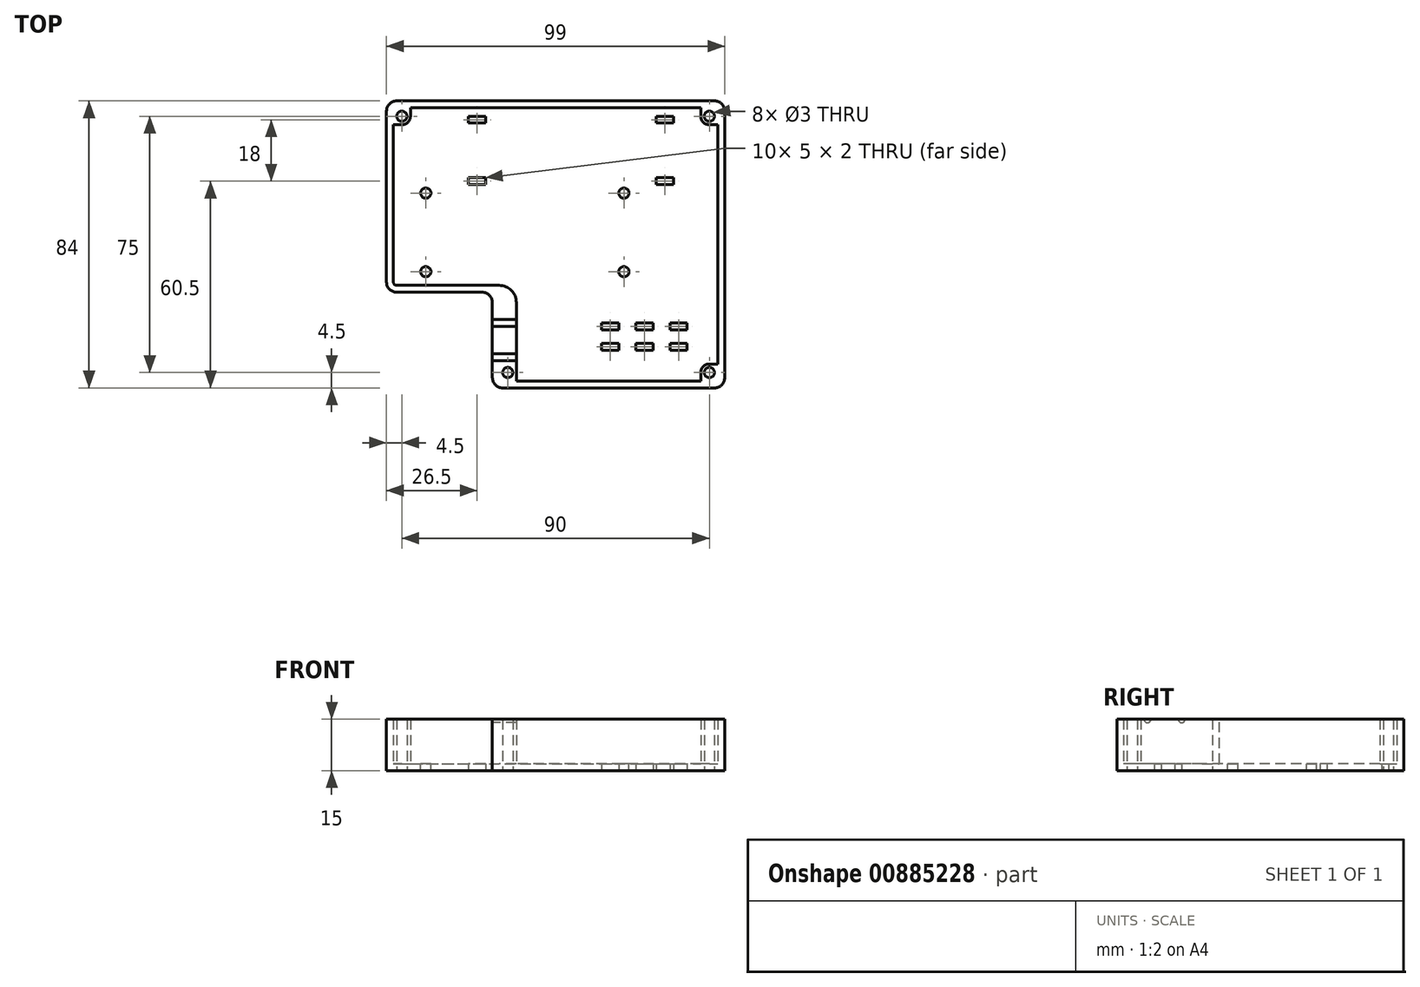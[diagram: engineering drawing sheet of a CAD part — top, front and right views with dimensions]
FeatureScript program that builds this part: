
annotation { "Feature Type Name" : "Feature", "Feature Type Description" : "" }
export const myFeature = defineFeature(function(context is Context, id is Id, definition is map)
    precondition{}
    {
        {
            var Q0;
            Q0=qCreatedBy(makeId("Top.planeOp"),FACE);
            var sketch = newSketch(context, id + "F0", { "sketchPlane" : qUnion([Q0])});
            skLineSegment(sketch, "E0.bottom", {"start": v(37.5, 17.5) * mm, "end": v(-37.5, 17.5) * mm});
            skLineSegment(sketch, "E0.left", {"start": v(40.5, 14.5) * mm, "end": v(40.5, -14.5) * mm});
            skLineSegment(sketch, "E0.right", {"start": v(-40.5, 14.5) * mm, "end": v(-40.5, -14.5) * mm});
            skPoint(sketch, "E0.middle", {"position": v(0, 0) * mm});
            skPoint(sketch, "E1.visualSharp", {"position": v(40.5, -17.5) * mm});
            skArc(sketch, "E1.filletArc", {"start": v(37.5, -17.5) * mm, "mid": v(39.62, -16.62) * mm, "end": v(40.5, -14.5) * mm});
            skPoint(sketch, "E2.visualSharp", {"position": v(40.5, 17.5) * mm});
            skArc(sketch, "E2.filletArc", {"start": v(40.5, 14.5) * mm, "mid": v(39.62, 16.62) * mm, "end": v(37.5, 17.5) * mm});
            skPoint(sketch, "E3.visualSharp", {"position": v(-40.5, -17.5) * mm});
            skArc(sketch, "E3.filletArc", {"start": v(-40.5, -14.5) * mm, "mid": v(-39.62, -16.62) * mm, "end": v(-37.5, -17.5) * mm});
            skPoint(sketch, "E4.visualSharp", {"position": v(-40.5, 17.5) * mm});
            skArc(sketch, "E4.filletArc", {"start": v(-37.5, 17.5) * mm, "mid": v(-39.62, 16.62) * mm, "end": v(-40.5, 14.5) * mm});
            skLineSegment(sketch, "E5", {"start": v(58.5, 35.5) * mm, "end": v(58.5, -42.5) * mm});
            skLineSegment(sketch, "E6", {"start": v(-37.5, 38.5) * mm, "end": v(55.5, 38.5) * mm});
            skLineSegment(sketch, "E7", {"start": v(55.5, -45.5) * mm, "end": v(-6.5, -45.5) * mm});
            skLineSegment(sketch, "E8", {"start": v(-9.5, -20.5) * mm, "end": v(-9.5, -42.5) * mm});
            skLineSegment(sketch, "E9", {"start": v(-40.5, 35.5) * mm, "end": v(-40.5, 14.5) * mm});
            skPoint(sketch, "E10.visualSharp", {"position": v(-40.5, 38.5) * mm});
            skArc(sketch, "E10.filletArc", {"start": v(-37.5, 38.5) * mm, "mid": v(-39.62, 37.62) * mm, "end": v(-40.5, 35.5) * mm});
            skPoint(sketch, "E11.visualSharp", {"position": v(58.5, 38.5) * mm});
            skArc(sketch, "E11.filletArc", {"start": v(58.5, 35.5) * mm, "mid": v(57.62, 37.62) * mm, "end": v(55.5, 38.5) * mm});
            skPoint(sketch, "E12.visualSharp", {"position": v(58.5, -45.5) * mm});
            skArc(sketch, "E12.filletArc", {"start": v(55.5, -45.5) * mm, "mid": v(57.62, -44.62) * mm, "end": v(58.5, -42.5) * mm});
            skPoint(sketch, "E13.visualSharp", {"position": v(-9.5, -45.5) * mm});
            skArc(sketch, "E13.filletArc", {"start": v(-9.5, -42.5) * mm, "mid": v(-8.62, -44.62) * mm, "end": v(-6.5, -45.5) * mm});
            skLineSegment(sketch, "E14", {"start": v(-9.5, -17.5) * mm, "end": v(37.5, -17.5) * mm, "construction": true});
            skLineSegment(sketch, "E15", {"start": v(-37.5, -17.5) * mm, "end": v(-12.5, -17.5) * mm});
            skPoint(sketch, "E16.visualSharp", {"position": v(-9.5, -17.5) * mm});
            skArc(sketch, "E16.filletArc", {"start": v(-9.5, -20.5) * mm, "mid": v(-10.38, -18.38) * mm, "end": v(-12.5, -17.5) * mm});
            skSolve(sketch);
        }
        {
            var Q0;
            Q0 = qSketchRegion(id + "F0", true);
            extrude(context, id + "F1", {"entities" : qUnion([Q0]), "depth" : 15 * mm, "offsetDistance" : 25 * mm});
        }
        {
            var Q0;
            Q0=makeQuery(id+"F1.opExtrude","CAP_FACE",FACE,{"disambiguationData":[OSD([sQuery(id+"F0.wireOp",EDGE,"E0.bottom"),sQuery(id+"F0.wireOp",EDGE,"E0.top"),sQuery(id+"F0.wireOp",EDGE,"E0.left"),sQuery(id+"F0.wireOp",EDGE,"E0.right")])],"isStart":false});
            shell(context, id + "F2", {"entities" : qUnion([Q0]), "thickness" : 2 * mm});
        }
        {
            var Q0;
            Q0=makeQuery(id+"F2.opShell","OFFSET_FACE",FACE,{"disambiguationData":[OSD([sQuery(id+"F0.wireOp",EDGE,"E0.top"),sQuery(id+"F0.wireOp",EDGE,"E0.right"),sQuery(id+"F0.wireOp",EDGE,"E3.filletArc"),sQuery(id+"F0.wireOp",EDGE,"E5"),sQuery(id+"F0.wireOp",EDGE,"E6"),sQuery(id+"F0.wireOp",EDGE,"E7"),sQuery(id+"F0.wireOp",EDGE,"E8"),sQuery(id+"F0.wireOp",EDGE,"E9")])]});
            var sketch = newSketch(context, id + "F3", { "sketchPlane" : qUnion([Q0])});
            skCircle(sketch, "E17", {"center": v(-29, 11.5) * mm, "radius": 1.5 * mm});
            skCircle(sketch, "E18.MirrorC", {"center": v(29, 11.5) * mm, "radius": 1.5 * mm});
            skCircle(sketch, "E19.MirrorC", {"center": v(-29, -11.5) * mm, "radius": 1.5 * mm});
            skCircle(sketch, "E20.MirrorC", {"center": v(29, -11.5) * mm, "radius": 1.5 * mm});
            skSolve(sketch);
        }
        {
            var Q0;
            Q0 = qSketchRegion(id + "F3", true);
            extrude(context, id + "F4", {"entities" : qUnion([Q0]), "operationType" : NewBodyOperationType.REMOVE, "endBound" : BoundingType.UP_TO_NEXT, "oppositeDirection" : true, "depth" : 2 * mm, "offsetDistance" : 25 * mm});
        }
        {
            var Q0;
            Q0=makeQuery(id+"F2.opShell","OFFSET_FACE",FACE,{"disambiguationData":[OSD([sQuery(id+"F0.wireOp",EDGE,"E0.right"),sQuery(id+"F0.wireOp",EDGE,"E3.filletArc"),sQuery(id+"F0.wireOp",EDGE,"E5"),sQuery(id+"F0.wireOp",EDGE,"E6"),sQuery(id+"F0.wireOp",EDGE,"E7"),sQuery(id+"F0.wireOp",EDGE,"E8"),sQuery(id+"F0.wireOp",EDGE,"E9"),sQuery(id+"F0.wireOp",EDGE,"E10.filletArc"),sQuery(id+"F0.wireOp",EDGE,"E11.filletArc"),sQuery(id+"F0.wireOp",EDGE,"E12.filletArc"),sQuery(id+"F0.wireOp",EDGE,"E13.filletArc"),sQuery(id+"F0.wireOp",EDGE,"E15"),sQuery(id+"F0.wireOp",EDGE,"E16.filletArc")])]});
            var sketch = newSketch(context, id + "F5", { "sketchPlane" : qUnion([Q0])});
            skCircle(sketch, "E21.0", {"center": v(-5, -41) * mm, "radius": 1.5 * mm});
            skLineSegment(sketch, "E22", {"start": v(-2.5, -41) * mm, "end": v(-2.5, -43.5) * mm});
            skLineSegment(sketch, "E23", {"start": v(24.5, -43.5) * mm, "end": v(24.5, -19.2) * mm, "construction": true});
            skLineSegment(sketch, "E24.MirrorCS", {"start": v(51.5, -41) * mm, "end": v(51.5, -43.5) * mm});
            skLineSegment(sketch, "E25.MirrorCS", {"start": v(54, -38.5) * mm, "end": v(56.5, -38.5) * mm});
            skCircle(sketch, "E26.MirrorC", {"center": v(54, -41) * mm, "radius": 1.5 * mm});
            skArc(sketch, "E27.MirrorCS", {"start": v(51.5, -41) * mm, "mid": v(52.23, -39.23) * mm, "end": v(54, -38.5) * mm});
            skLineSegment(sketch, "E28", {"start": v(56.5, -3.5) * mm, "end": v(28.34, -3.5) * mm, "construction": true});
            skLineSegment(sketch, "E29.MirrorCS", {"start": v(54, 31.5) * mm, "end": v(56.5, 31.5) * mm});
            skArc(sketch, "E30.MirrorCS", {"start": v(51.5, 34) * mm, "mid": v(52.23, 32.23) * mm, "end": v(54, 31.5) * mm});
            skLineSegment(sketch, "E31.MirrorCS", {"start": v(51.5, 34) * mm, "end": v(51.5, 36.5) * mm});
            skCircle(sketch, "E32.MirrorC", {"center": v(54, 34) * mm, "radius": 1.5 * mm});
            skLineSegment(sketch, "E33", {"start": v(9, 36.5) * mm, "end": v(9, 20.74) * mm, "construction": true});
            skLineSegment(sketch, "E34.MirrorCS", {"start": v(-36, 31.5) * mm, "end": v(-38.5, 31.5) * mm});
            skArc(sketch, "E35.MirrorCS", {"start": v(-33.5, 34) * mm, "mid": v(-34.23, 32.23) * mm, "end": v(-36, 31.5) * mm});
            skLineSegment(sketch, "E36.MirrorCS", {"start": v(-33.5, 34) * mm, "end": v(-33.5, 36.5) * mm});
            skCircle(sketch, "E37.MirrorC", {"center": v(-36, 34) * mm, "radius": 1.5 * mm});
            skLineSegment(sketch, "E38", {"start": v(-7.5, -38.5) * mm, "end": v(-7.5, -43.5) * mm});
            skLineSegment(sketch, "E39", {"start": v(-7.5, -43.5) * mm, "end": v(-2.5, -43.5) * mm});
            skLineSegment(sketch, "E40.MirrorCS", {"start": v(56.5, -38.5) * mm, "end": v(56.5, -43.5) * mm});
            skLineSegment(sketch, "E41.MirrorCS", {"start": v(56.5, -43.5) * mm, "end": v(51.5, -43.5) * mm});
            skLineSegment(sketch, "E42.MirrorCS", {"start": v(56.5, 31.5) * mm, "end": v(56.5, 36.5) * mm});
            skLineSegment(sketch, "E43.MirrorCS", {"start": v(56.5, 36.5) * mm, "end": v(51.5, 36.5) * mm});
            skLineSegment(sketch, "E44.MirrorCS", {"start": v(-38.5, 31.5) * mm, "end": v(-38.5, 36.5) * mm});
            skLineSegment(sketch, "E45.MirrorCS", {"start": v(-38.5, 36.5) * mm, "end": v(-33.5, 36.5) * mm});
            skLineSegment(sketch, "E46", {"start": v(-2.5, -41) * mm, "end": v(-2.5, -20.5) * mm});
            skLineSegment(sketch, "E47", {"start": v(-7.5, -15.5) * mm, "end": v(-12.5, -15.5) * mm});
            skLineSegment(sketch, "E48", {"start": v(-12.5, -15.5) * mm, "end": v(-7.5, -20.5) * mm});
            skLineSegment(sketch, "E49", {"start": v(-7.5, -20.5) * mm, "end": v(-7.5, -38.5) * mm});
            skPoint(sketch, "E50.visualSharp", {"position": v(-2.5, -15.5) * mm});
            skArc(sketch, "E50.filletArc", {"start": v(-2.5, -20.5) * mm, "mid": v(-3.96, -16.96) * mm, "end": v(-7.5, -15.5) * mm});
            skSolve(sketch);
        }
        {
            var Q0;
            Q0 = qSketchRegion(id + "F5", true);
            var Q1;
            {var subQ0=sQuery(id+"F0.wireOp",EDGE,"E13.filletArc");var subQ1=sQuery(id+"F0.wireOp",EDGE,"E12.filletArc");var subQ2=sQuery(id+"F0.wireOp",EDGE,"E11.filletArc");var subQ3=sQuery(id+"F0.wireOp",EDGE,"E10.filletArc");var subQ4=sQuery(id+"F0.wireOp",EDGE,"E8");var subQ5=sQuery(id+"F0.wireOp",EDGE,"E7");var subQ6=sQuery(id+"F0.wireOp",EDGE,"E6");var subQ7=sQuery(id+"F0.wireOp",EDGE,"E16.filletArc");var subQ8=sQuery(id+"F0.wireOp",EDGE,"E5");var subQ9=sQuery(id+"F0.wireOp",EDGE,"E15");var subQ10=sQuery(id+"F0.wireOp",EDGE,"E3.filletArc");var subQ11=sQuery(id+"F0.wireOp",EDGE,"E9");var subQ12=sQuery(id+"F0.wireOp",EDGE,"E0.right");Q1=makeQuery(id+"F12.boolean.opBoolean","SPLIT",FACE,{"disambiguationData":[TD([makeQuery(id+"F1.opExtrude","SWEPT_FACE",FACE,{"disambiguationData":[OSD([subQ12,subQ11])]}),makeQuery(id+"F1.opExtrude","SWEPT_FACE",FACE,{"disambiguationData":[OSD([subQ10])]}),makeQuery(id+"F1.opExtrude","SWEPT_FACE",FACE,{"disambiguationData":[OSD([subQ8])]}),makeQuery(id+"F1.opExtrude","SWEPT_FACE",FACE,{"disambiguationData":[OSD([subQ6])]}),makeQuery(id+"F1.opExtrude","SWEPT_FACE",FACE,{"disambiguationData":[OSD([subQ5])]}),makeQuery(id+"F1.opExtrude","SWEPT_FACE",FACE,{"disambiguationData":[OSD([subQ4])]}),makeQuery(id+"F1.opExtrude","SWEPT_FACE",FACE,{"disambiguationData":[OSD([subQ3])]}),makeQuery(id+"F1.opExtrude","SWEPT_FACE",FACE,{"disambiguationData":[OSD([subQ2])]}),makeQuery(id+"F1.opExtrude","SWEPT_FACE",FACE,{"disambiguationData":[OSD([subQ1])]}),makeQuery(id+"F1.opExtrude","SWEPT_FACE",FACE,{"disambiguationData":[OSD([subQ0])]}),makeQuery(id+"F1.opExtrude","SWEPT_FACE",FACE,{"disambiguationData":[OSD([subQ9])]}),makeQuery(id+"F1.opExtrude","SWEPT_FACE",FACE,{"disambiguationData":[OSD([subQ7])]}),makeQuery(id+"F2.opShell","OFFSET_FACE",FACE,{"disambiguationData":[OSD([subQ12,subQ11])]}),makeQuery(id+"F2.opShell","OFFSET_FACE",FACE,{"disambiguationData":[OSD([subQ10])]}),makeQuery(id+"F2.opShell","OFFSET_FACE",FACE,{"disambiguationData":[OSD([subQ8])]}),makeQuery(id+"F2.opShell","OFFSET_FACE",FACE,{"disambiguationData":[OSD([subQ6])]}),makeQuery(id+"F2.opShell","OFFSET_FACE",FACE,{"disambiguationData":[OSD([subQ5])]}),makeQuery(id+"F2.opShell","OFFSET_FACE",FACE,{"disambiguationData":[OSD([subQ4])]}),makeQuery(id+"F2.opShell","OFFSET_FACE",FACE,{"disambiguationData":[OSD([subQ3])]}),makeQuery(id+"F2.opShell","OFFSET_FACE",FACE,{"disambiguationData":[OSD([subQ2])]}),makeQuery(id+"F2.opShell","OFFSET_FACE",FACE,{"disambiguationData":[OSD([subQ1])]}),makeQuery(id+"F2.opShell","OFFSET_FACE",FACE,{"disambiguationData":[OSD([subQ0])]}),makeQuery(id+"F2.opShell","OFFSET_FACE",FACE,{"disambiguationData":[OSD([subQ9])]}),makeQuery(id+"F2.opShell","OFFSET_FACE",FACE,{"disambiguationData":[OSD([subQ7])]}),makeQuery(id+"F12.opExtrude","SWEPT_FACE",FACE,{"disambiguationData":[OSD([sQuery(id+"F11.wireOp",EDGE,"E77")])]}),makeQuery(id+"F12.opExtrude","SWEPT_FACE",FACE,{"disambiguationData":[OSD([sQuery(id+"F11.wireOp",EDGE,"E78")])]})])],"derivedFrom":makeQuery(id+"F1.opExtrude","CAP_FACE",FACE,{"disambiguationData":[OSD([subQ12,subQ10,subQ8,subQ6,subQ5,subQ4,subQ11,subQ3,subQ2,subQ1,subQ0,subQ9,subQ7])],"isStart":false})});}
            extrude(context, id + "F6", {"entities" : qUnion([Q0]), "operationType" : NewBodyOperationType.ADD, "endBound" : BoundingType.UP_TO_SURFACE, "depth" : 25 * mm, "endBoundEntityFace" : qUnion([Q1]), "offsetDistance" : 25 * mm});
        }
        {
            var Q0;
            Q0=qCreatedBy(makeId("Top.planeOp"),FACE);
            var sketch = newSketch(context, id + "F7", { "sketchPlane" : qUnion([Q0])});
            skLineSegment(sketch, "E51.bottom", {"start": v(-11.5, 32) * mm, "end": v(-16.5, 32) * mm});
            skLineSegment(sketch, "E51.top", {"start": v(-11.5, 34) * mm, "end": v(-16.5, 34) * mm});
            skLineSegment(sketch, "E51.left", {"start": v(-11.5, 32) * mm, "end": v(-11.5, 34) * mm});
            skLineSegment(sketch, "E51.right", {"start": v(-16.5, 32) * mm, "end": v(-16.5, 34) * mm});
            skPoint(sketch, "E51.middle", {"position": v(-14, 33) * mm});
            skLineSegment(sketch, "E52.bottom", {"start": v(-26.5, 16.5) * mm, "end": v(53.5, 16.5) * mm, "construction": true});
            skLineSegment(sketch, "E52.top", {"start": v(-26.5, 31.5) * mm, "end": v(53.5, 31.5) * mm, "construction": true});
            skLineSegment(sketch, "E52.left", {"start": v(-26.5, 16.5) * mm, "end": v(-26.5, 31.5) * mm, "construction": true});
            skLineSegment(sketch, "E52.right", {"start": v(53.5, 16.5) * mm, "end": v(53.5, 31.5) * mm, "construction": true});
            skLineSegment(sketch, "E53", {"start": v(13.5, 16.5) * mm, "end": v(13.5, 31.5) * mm, "construction": true});
            skLineSegment(sketch, "E54", {"start": v(53.5, 24) * mm, "end": v(-26.5, 24) * mm, "construction": true});
            skLineSegment(sketch, "E55.MirrorCS", {"start": v(38.5, 34) * mm, "end": v(43.5, 34) * mm});
            skLineSegment(sketch, "E56.MirrorCS", {"start": v(38.5, 32) * mm, "end": v(38.5, 34) * mm});
            skLineSegment(sketch, "E57.MirrorCS", {"start": v(38.5, 32) * mm, "end": v(43.5, 32) * mm});
            skLineSegment(sketch, "E58.MirrorCS", {"start": v(43.5, 32) * mm, "end": v(43.5, 34) * mm});
            skLineSegment(sketch, "E59.MirrorCS", {"start": v(38.5, 14) * mm, "end": v(43.5, 14) * mm});
            skLineSegment(sketch, "E60.MirrorCS", {"start": v(38.5, 16) * mm, "end": v(43.5, 16) * mm});
            skLineSegment(sketch, "E61.MirrorCS", {"start": v(43.5, 16) * mm, "end": v(43.5, 14) * mm});
            skLineSegment(sketch, "E62.MirrorCS", {"start": v(38.5, 16) * mm, "end": v(38.5, 14) * mm});
            skLineSegment(sketch, "E63.MirrorCS", {"start": v(-11.5, 16) * mm, "end": v(-11.5, 14) * mm});
            skLineSegment(sketch, "E64.MirrorCS", {"start": v(-11.5, 14) * mm, "end": v(-16.5, 14) * mm});
            skLineSegment(sketch, "E65.MirrorCS", {"start": v(-16.5, 16) * mm, "end": v(-16.5, 14) * mm});
            skLineSegment(sketch, "E66.MirrorCS", {"start": v(-11.5, 16) * mm, "end": v(-16.5, 16) * mm});
            skLineSegment(sketch, "E67.bottom", {"start": v(22.5, -28.5) * mm, "end": v(27.5, -28.5) * mm});
            skLineSegment(sketch, "E67.top", {"start": v(22.5, -26.5) * mm, "end": v(27.5, -26.5) * mm});
            skLineSegment(sketch, "E67.left", {"start": v(22.5, -28.5) * mm, "end": v(22.5, -26.5) * mm});
            skLineSegment(sketch, "E67.right", {"start": v(27.5, -28.5) * mm, "end": v(27.5, -26.5) * mm});
            skLineSegment(sketch, "E68.bottom", {"start": v(22.5, -34.5) * mm, "end": v(27.5, -34.5) * mm});
            skLineSegment(sketch, "E68.top", {"start": v(22.5, -32.5) * mm, "end": v(27.5, -32.5) * mm});
            skLineSegment(sketch, "E68.left", {"start": v(22.5, -34.5) * mm, "end": v(22.5, -32.5) * mm});
            skLineSegment(sketch, "E68.right", {"start": v(27.5, -34.5) * mm, "end": v(27.5, -32.5) * mm});
            skLineSegment(sketch, "E69.bottom", {"start": v(32.5, -28.5) * mm, "end": v(37.5, -28.5) * mm});
            skLineSegment(sketch, "E69.top", {"start": v(32.5, -26.5) * mm, "end": v(37.5, -26.5) * mm});
            skLineSegment(sketch, "E69.left", {"start": v(32.5, -28.5) * mm, "end": v(32.5, -26.5) * mm});
            skLineSegment(sketch, "E69.right", {"start": v(37.5, -28.5) * mm, "end": v(37.5, -26.5) * mm});
            skLineSegment(sketch, "E70.bottom", {"start": v(32.5, -34.5) * mm, "end": v(37.5, -34.5) * mm});
            skLineSegment(sketch, "E70.top", {"start": v(32.5, -32.5) * mm, "end": v(37.5, -32.5) * mm});
            skLineSegment(sketch, "E70.left", {"start": v(32.5, -34.5) * mm, "end": v(32.5, -32.5) * mm});
            skLineSegment(sketch, "E70.right", {"start": v(37.5, -34.5) * mm, "end": v(37.5, -32.5) * mm});
            skLineSegment(sketch, "E71.bottom", {"start": v(42.5, -28.5) * mm, "end": v(47.5, -28.5) * mm});
            skLineSegment(sketch, "E71.top", {"start": v(42.5, -26.5) * mm, "end": v(47.5, -26.5) * mm});
            skLineSegment(sketch, "E71.left", {"start": v(42.5, -28.5) * mm, "end": v(42.5, -26.5) * mm});
            skLineSegment(sketch, "E71.right", {"start": v(47.5, -28.5) * mm, "end": v(47.5, -26.5) * mm});
            skLineSegment(sketch, "E72.bottom", {"start": v(42.5, -34.5) * mm, "end": v(47.5, -34.5) * mm});
            skLineSegment(sketch, "E72.top", {"start": v(42.5, -32.5) * mm, "end": v(47.5, -32.5) * mm});
            skLineSegment(sketch, "E72.left", {"start": v(42.5, -34.5) * mm, "end": v(42.5, -32.5) * mm});
            skLineSegment(sketch, "E72.right", {"start": v(47.5, -34.5) * mm, "end": v(47.5, -32.5) * mm});
            skSolve(sketch);
        }
        {
            var Q0;
            Q0 = qSketchRegion(id + "F7", true);
            extrude(context, id + "F8", {"entities" : qUnion([Q0]), "operationType" : NewBodyOperationType.REMOVE, "endBound" : BoundingType.UP_TO_NEXT, "depth" : 25 * mm, "offsetDistance" : 25 * mm});
        }
        {
            var Q0;
            {var subQ0=sQuery(id+"F0.wireOp",EDGE,"E15");var subQ1=sQuery(id+"F0.wireOp",EDGE,"E7");var subQ2=sQuery(id+"F0.wireOp",EDGE,"E9");var subQ3=sQuery(id+"F0.wireOp",EDGE,"E0.right");var subQ4=sQuery(id+"F0.wireOp",EDGE,"E3.filletArc");var subQ5=sQuery(id+"F0.wireOp",EDGE,"E5");var subQ6=sQuery(id+"F0.wireOp",EDGE,"E6");Q0=makeQuery(id+"F6.boolean.opBoolean","SPLIT",FACE,{"disambiguationData":[TD([makeQuery(id+"F2.opShell","OFFSET_FACE",FACE,{"disambiguationData":[OSD([subQ4])]})])],"derivedFrom":makeQuery(id+"F2.opShell","OFFSET_FACE",FACE,{"disambiguationData":[OSD([subQ3,subQ4,subQ5,subQ6,subQ1,sQuery(id+"F0.wireOp",EDGE,"E8"),subQ2,sQuery(id+"F0.wireOp",EDGE,"E10.filletArc"),sQuery(id+"F0.wireOp",EDGE,"E11.filletArc"),sQuery(id+"F0.wireOp",EDGE,"E12.filletArc"),sQuery(id+"F0.wireOp",EDGE,"E13.filletArc"),subQ0,sQuery(id+"F0.wireOp",EDGE,"E16.filletArc")])]})});}
            var sketch = newSketch(context, id + "F9", { "sketchPlane" : qUnion([Q0])});
            skCircle(sketch, "E73.0", {"center": v(54, 34) * mm, "radius": 1.5 * mm});
            skCircle(sketch, "E74.0", {"center": v(-36, 34) * mm, "radius": 1.5 * mm});
            skCircle(sketch, "E75.0", {"center": v(-5, -41) * mm, "radius": 1.5 * mm});
            skCircle(sketch, "E76.0", {"center": v(54, -41) * mm, "radius": 1.5 * mm});
            skSolve(sketch);
        }
        {
            var Q0;
            Q0 = qSketchRegion(id + "F9", true);
            extrude(context, id + "F10", {"entities" : qUnion([Q0]), "operationType" : NewBodyOperationType.REMOVE, "endBound" : BoundingType.UP_TO_NEXT, "oppositeDirection" : true, "depth" : 25 * mm, "offsetDistance" : 25 * mm});
        }
        {
            var Q0;
            Q0=makeQuery(id+"F1.opExtrude","SWEPT_FACE",FACE,{"disambiguationData":[OSD([sQuery(id+"F0.wireOp",EDGE,"E8")])]});
            var sketch = newSketch(context, id + "F11", { "sketchPlane" : qUnion([Q0])});
            skCircle(sketch, "E77", {"center": v(26.5, 15) * mm, "radius": 1 * mm});
            skCircle(sketch, "E78", {"center": v(36.5, 15) * mm, "radius": 1 * mm});
            skSolve(sketch);
        }
        {
            var Q0;
            Q0 = qSketchRegion(id + "F11", true);
            extrude(context, id + "F12", {"entities" : qUnion([Q0]), "operationType" : NewBodyOperationType.REMOVE, "endBound" : BoundingType.UP_TO_NEXT, "oppositeDirection" : true, "depth" : 25 * mm, "offsetDistance" : 25 * mm});
        }
    });
